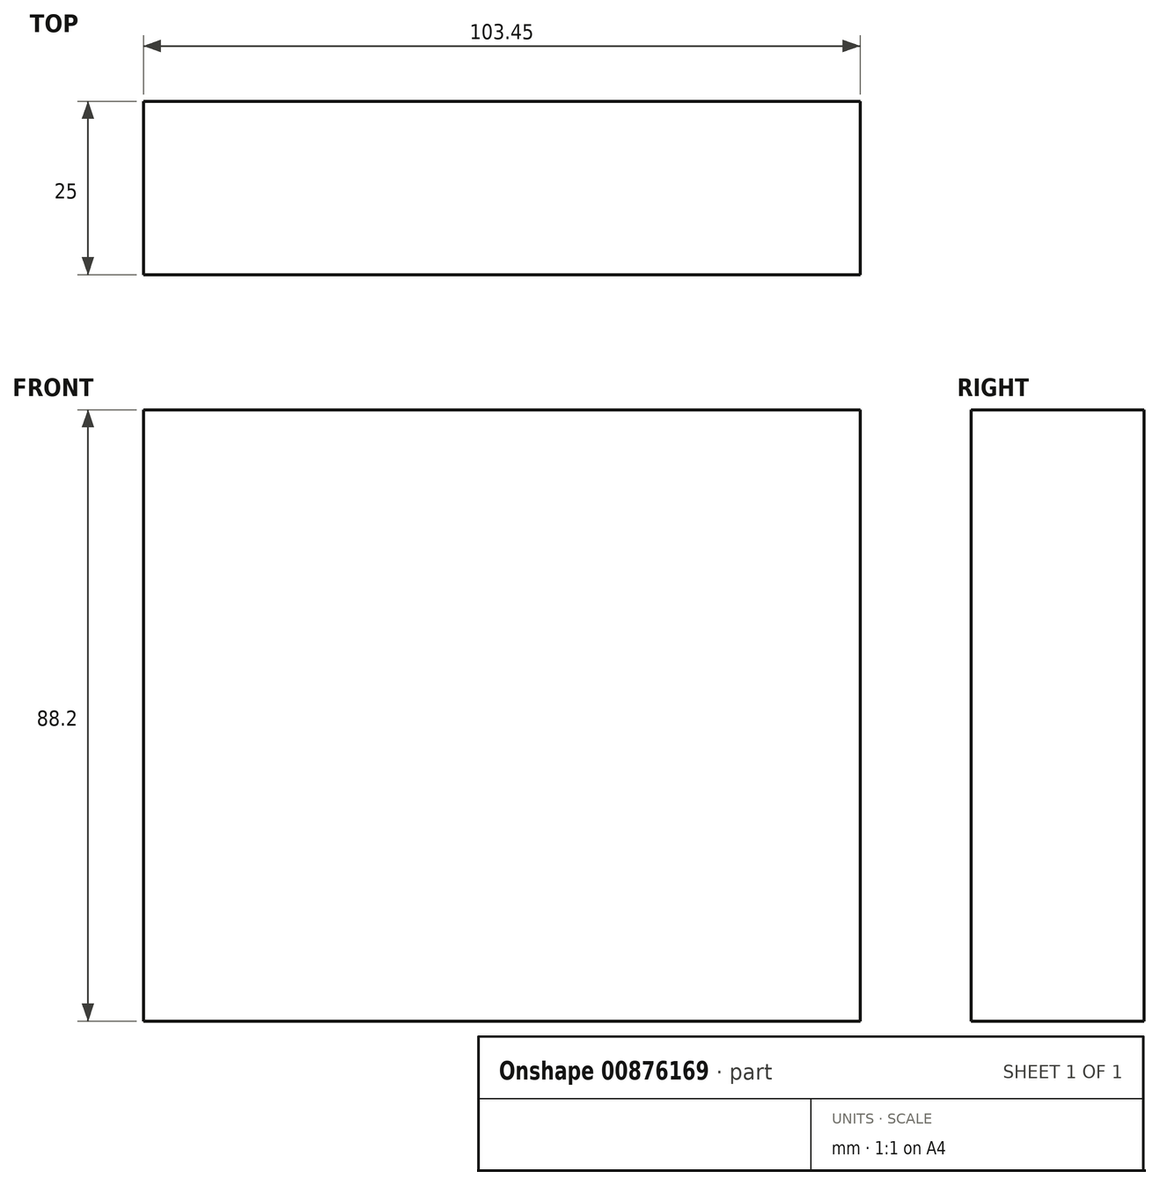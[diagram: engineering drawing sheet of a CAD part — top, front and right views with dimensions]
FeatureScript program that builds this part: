
annotation { "Feature Type Name" : "Feature", "Feature Type Description" : "" }
export const myFeature = defineFeature(function(context is Context, id is Id, definition is map)
    precondition{}
    {
        {
            var Q0;
            Q0=qCreatedBy(makeId("Front.planeOp"),FACE);
            var sketch = newSketch(context, id + "F0", { "sketchPlane" : qUnion([Q0])});
            skLineSegment(sketch, "E0.bottom", {"start": v(-196.24, 20.06) * mm, "end": v(-92.79, 20.06) * mm});
            skLineSegment(sketch, "E0.top", {"start": v(-196.24, -68.14) * mm, "end": v(-92.79, -68.14) * mm});
            skLineSegment(sketch, "E0.left", {"start": v(-196.24, 20.06) * mm, "end": v(-196.24, -68.14) * mm});
            skLineSegment(sketch, "E0.right", {"start": v(-92.79, 20.06) * mm, "end": v(-92.79, -68.14) * mm});
            skSolve(sketch);
        }
        {
            var Q0;
            Q0 = qSketchRegion(id + "F0", true);
            extrude(context, id + "F1", {"entities" : qUnion([Q0]), "depth" : 25 * mm, "offsetDistance" : 25 * mm});
        }
    });
